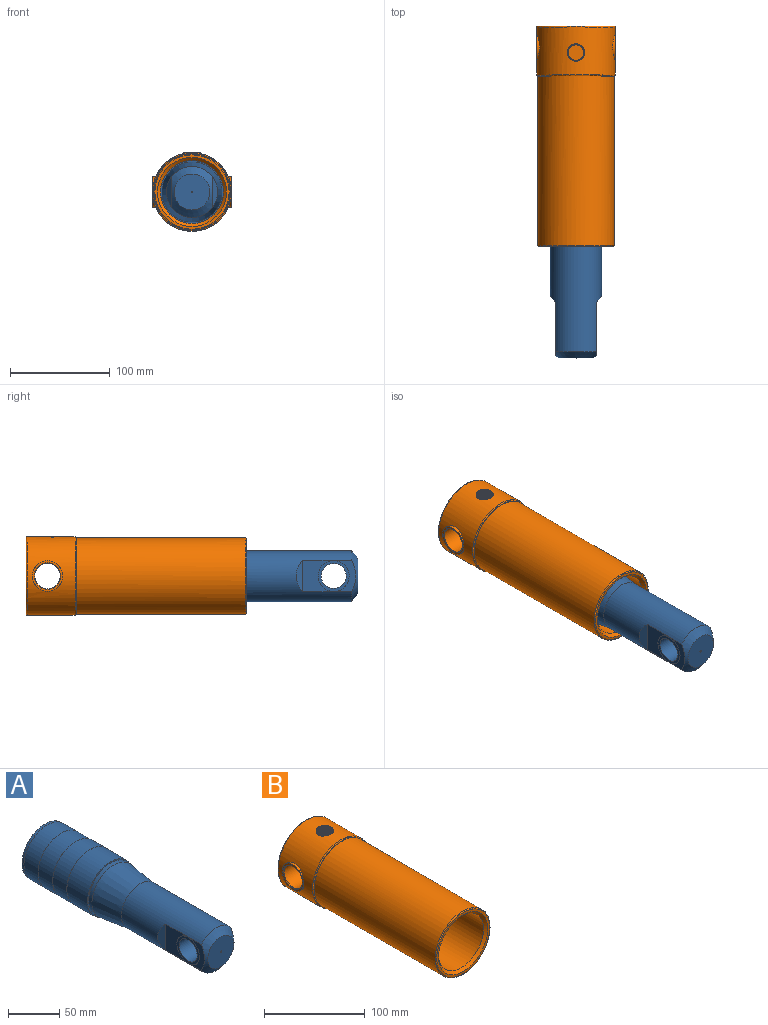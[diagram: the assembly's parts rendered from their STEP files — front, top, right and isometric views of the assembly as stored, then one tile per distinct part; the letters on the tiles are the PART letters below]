
ASSEMBLY  parts=2 mates=1
PART A: 32 faces, bbox 63.2x242.5x63.2 mm
  f0: cylinder r=31.5mm len=63mm, axis (0,-1,0), area 5660.5mm2, adj f4,f5
  f1: cylinder r=31.5mm len=63mm, axis (0,-1,0), area 3998mm2, adj f2,f29
  f2: plane 63.2x63.2mm, normal (0,1,0), area 19.8mm2, adj f1,f3
  f3: cylinder r=31.6mm len=63.2mm, axis (0,-1,0), area 3851.8mm2, adj f2,f4
  f4: plane 63.2x63.2mm, normal (0,-1,0), area 19.8mm2, adj f0,f3
  f5: plane 63x63mm, normal (0,-1,0), area 289.8mm2, adj f0,f26
  f6: plane 27.05x27.05mm, normal (-1,0,0), area 81.8mm2, adj f8,f9
  f7: plane 27.05x27.05mm, normal (1,0,0), area 81.8mm2, adj f9,f10
  f8: cylinder r=12.53mm len=25.05mm, axis (-1,0,0), area 1550.3mm2, adj f6,f11
  f9: cylinder r=13.53mm len=27.05mm, axis (-1,0,0), area 167.4mm2, adj f6,f7,f12
  f10: cylinder r=12.53mm len=25.05mm, axis (-1,0,0), area 1550.3mm2, adj f7,f13
  f11: plane 30.85x30.85mm, normal (1,0,0), area 254.6mm2, adj f8,f14
  f12: cylinder r=1mm len=10.79mm, axis (0,-1,0), area 67.6mm2, adj f9,f15
  f13: plane 30.85x30.85mm, normal (-1,0,0), area 254.6mm2, adj f10,f16
  f14: cylinder r=15.42mm len=30.85mm, axis (-1,0,0), area 41.2mm2, adj f11,f21
  f15: plane 35.8x35.8mm, normal (0,-1,0), area 1003.5mm2, adj f12,f22
  f16: cylinder r=15.42mm len=30.85mm, axis (-1,0,0), area 41.2mm2, adj f13,f23
  f17: plane 3.2x0.05mm, normal (0,-1,0), area 0.1mm2, adj f18,f24
  f18: plane 31.1x6.23mm, normal (-0.77,-0.64,0), area 173.8mm2, adj f17,f23,f24
  f19: plane 3.2x0.05mm, normal (0,-1,0), area 0.1mm2, adj f20,f24
  f20: plane 31.1x6.23mm, normal (0.77,-0.64,0), area 173.8mm2, adj f19,f21,f24
  f21: plane 53.37x31.12mm, normal (1,0,0), area 863.6mm2, adj f14,f20,f22,f24
  f22: cone r=17.9mm half-angle=50deg, axis (0,1,0), area 1071.2mm2, adj f15,f21,f23,f24
  f23: plane 53.37x31.12mm, normal (-1,0,0), area 863.6mm2, adj f16,f18,f22,f24
  f24: cylinder r=25.55mm len=105.08mm, axis (0,-1,0), area 13319.9mm2, adj f17,f18,f19,f20,f21,f22,f23,f25
  f25: cone r=25.55mm half-angle=7deg, axis (0,1,0), area 6330.4mm2, adj f24,f26
  f26: cylinder r=30mm len=60mm, axis (0,-1,0), area 867.1mm2, adj f5,f25
  f27: plane 63.2x63.2mm, normal (0,1,0), area 19.8mm2, adj f28,f31
  f28: cylinder r=31.6mm len=63.2mm, axis (0,-1,0), area 3851.8mm2, adj f27,f29
  f29: plane 63.2x63.2mm, normal (0,-1,0), area 19.8mm2, adj f1,f28
  f30: plane 63x63mm, normal (0,1,0), area 3117.2mm2, adj f31
  f31: cylinder r=31.5mm len=63mm, axis (0,-1,0), area 554.2mm2, adj f27,f30
PART B: 47 faces, bbox 89.3x224.3x89.3 mm
  f0: cylinder r=15.15mm len=30.3mm, axis (1,0,0), area 0mm2, adj f1,f46
  f1: cylinder r=39.5mm len=79mm, axis (0,-1,0), area 10209.5mm2, adj f0,f2,f27,f28,f29,f30,f31,f42
  f2: cylinder r=8.59mm len=0.18mm, axis (0,0,1), area 0mm2, adj f1,f3,f29
  f3: plane 17.66x17.66mm, normal (0,0,1), area 25.2mm2, adj f2,f4,f25,f26,f27,f29,f30
  f4: bspline ~19.77x17.12mm, area 312.8mm2, adj f3,f5,f19,f20,f21,f22,f23,f24
  f5: cylinder r=7.75mm len=15.5mm, axis (0,0,1), area 28.8mm2, adj f4,f6,f18,f24
  f6: cylinder r=7.75mm len=15.5mm, axis (0,0,1), area 547.6mm2, adj f5,f7,f15,f17,f18,f19
  f7: cylinder r=5mm len=15.75mm, axis (0,-1,0), area 494.8mm2, adj f6,f8
  f8: plane 63x63mm, normal (0,-1,0), area 3038.7mm2, adj f7,f9
  f9: cylinder r=31.5mm len=167.5mm, axis (0,-1,0), area 33151.7mm2, adj f8,f10
  f10: cone r=31.5mm half-angle=45deg, axis (0,-1,0), area 879.7mm2, adj f9,f11
  f11: plane 74.2x74.2mm, normal (0,-1,0), area 584.8mm2, adj f10,f12
  f12: torus R=37.1mm, axis (0,1,0), area 372.4mm2, adj f11,f13
  f13: cylinder r=38.1mm len=169.5mm, axis (0,-1,0), area 40576.5mm2, adj f12,f14
  f14: plane 77x77mm, normal (0,-1,0), area 96.3mm2, adj f13,f44
  f15: plane 0.27x0.11mm, normal (0,1,0), area 0mm2, adj f6,f16,f18,f19
  f16: bspline ~16.83x16.46mm, area 11.2mm2, adj f15,f18,f19,f29
  f17: plane 15.5x15.5mm, normal (0,0,1), area 188.7mm2, adj f6
  f18: bspline ~16.82x16.51mm, area 25.4mm2, adj f5,f6,f15,f16,f26
  f19: bspline ~16.82x16.51mm, area 25.4mm2, adj f4,f6,f15,f16
  f20: cylinder r=7.75mm len=15.5mm, axis (0,0,1), area 18.2mm2, adj f4,f21,f25,f26
  f21: cylinder r=7.75mm len=15.5mm, axis (0,0,1), area 18.2mm2, adj f4,f20,f22,f26
  f22: cylinder r=7.75mm len=15.5mm, axis (0,0,1), area 18.3mm2, adj f4,f21,f23,f26
  f23: cylinder r=7.75mm len=15.5mm, axis (0,0,1), area 18.3mm2, adj f4,f22,f24,f26
  f24: cylinder r=7.75mm len=15.5mm, axis (0,0,1), area 18.3mm2, adj f4,f5,f23,f26
  f25: cylinder r=7.75mm len=15.5mm, axis (0,0,1), area 14.5mm2, adj f3,f4,f20,f26
  f26: bspline ~19.77x17.12mm, area 292.3mm2, adj f3,f18,f20,f21,f22,f23,f24,f25
  f27: cylinder r=8.59mm len=16.92mm, axis (0,0,1), area 0.7mm2, adj f1,f3,f29
  f28: cylinder r=8.59mm len=12.24mm, axis (0,0,1), area 0mm2, adj f1,f29
  f29: bspline ~19.93x17.26mm, area 71.6mm2, adj f1,f2,f3,f4,f16,f26,f27,f28
  f30: cylinder r=8.59mm len=17.19mm, axis (0,0,1), area 7.5mm2, adj f1,f3,f29
  f31: cylinder r=15.15mm len=30.3mm, axis (1,0,0), area 0mm2, adj f1,f32
  f32: plane 34.09x34.09mm, normal (-1,0,0), area 169.5mm2, adj f31,f33,f42
  f33: cone r=13.25mm half-angle=45deg, axis (-1,0,0), area 57.8mm2, adj f32,f34
  f34: cylinder r=12.75mm len=25.5mm, axis (1,0,0), area 1482mm2, adj f33,f35
  f35: plane 30.3x30.3mm, normal (1,0,0), area 210.4mm2, adj f34,f36
  f36: cylinder r=15.15mm len=41mm, axis (1,0,0), area 3883.1mm2, adj f35,f37,f39
  f37: cylinder r=2.5mm len=6.51mm, axis (0,1,0), area 102.2mm2, adj f36,f38
  f38: plane 77x77mm, normal (0,1,0), area 4637mm2, adj f37,f45
  f39: plane 30.3x30.3mm, normal (-1,0,0), area 210.4mm2, adj f36,f40
  f40: cylinder r=12.75mm len=25.5mm, axis (1,0,0), area 1482mm2, adj f39,f41
  f41: cone r=12.75mm half-angle=45deg, axis (1,0,0), area 57.8mm2, adj f40,f46
  f42: cylinder r=15.15mm len=30.3mm, axis (1,0,0), area 0mm2, adj f1,f32
  f43: cylinder r=15.15mm len=30.3mm, axis (1,0,0), area 0mm2, adj f1,f46
  f44: torus R=38.5mm, axis (0,1,0), area 386.3mm2, adj f1,f14
  f45: torus R=38.5mm, axis (0,-1,0), area 386.3mm2, adj f1,f38
  f46: plane 34.09x34.09mm, normal (1,0,0), area 169.5mm2, adj f0,f41,f43
PLACE A t=(0,-101.25,0)mm
PLACE B at identity fixed
MATE slider A.f0 <-> B.f1  axis (0,1,0) through (0,78.75,0)mm
